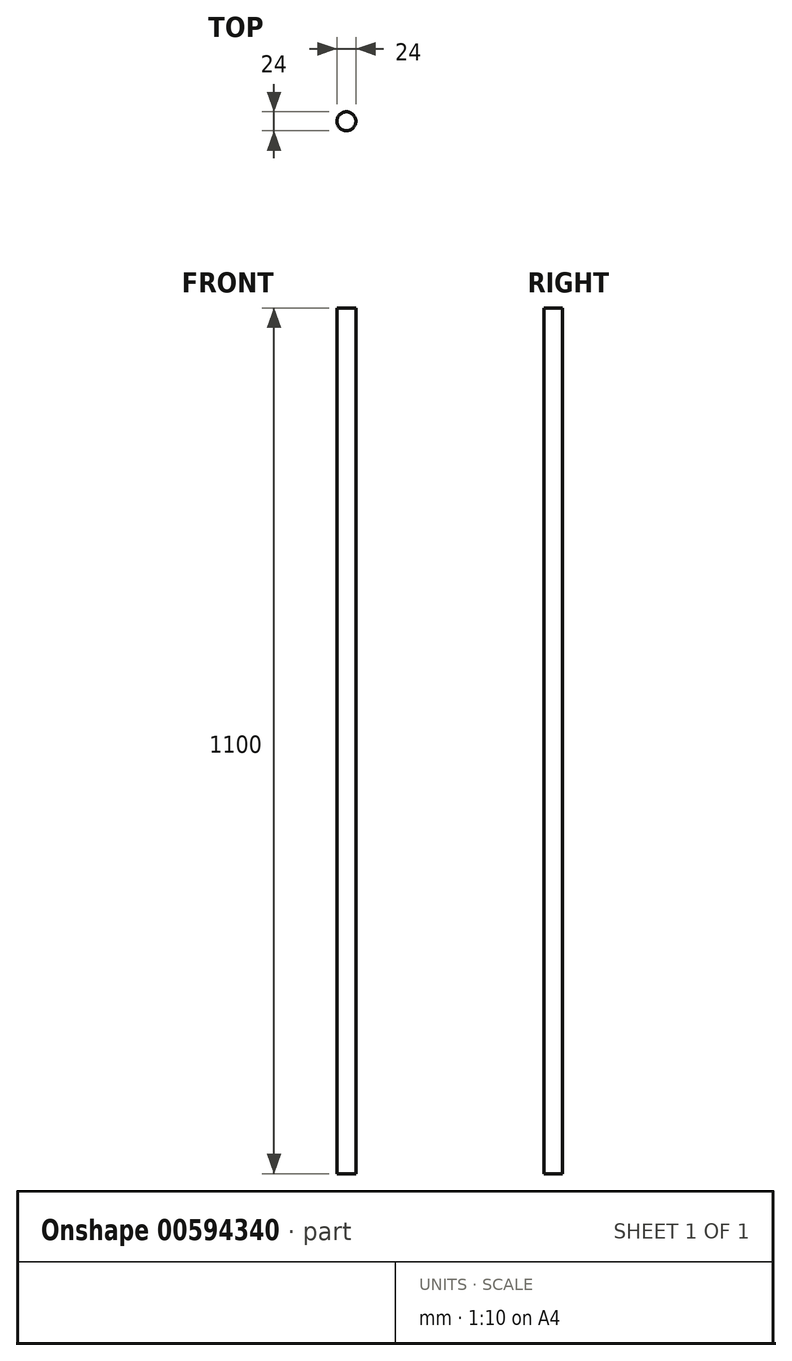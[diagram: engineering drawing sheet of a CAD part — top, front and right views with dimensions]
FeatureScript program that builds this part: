
annotation { "Feature Type Name" : "Feature", "Feature Type Description" : "" }
export const myFeature = defineFeature(function(context is Context, id is Id, definition is map)
    precondition{}
    {
        {
            var Q0;
            Q0=qCreatedBy(makeId("Top.planeOp"),FACE);
            var sketch = newSketch(context, id + "F0", { "sketchPlane" : qUnion([Q0])});
            skCircle(sketch, "E0", {"center": v(0, 0) * mm, "radius": 12 * mm});
            skSolve(sketch);
        }
        {
            var Q0;
            Q0 = qSketchRegion(id + "F0", true);
            extrude(context, id + "F1", {"entities" : qUnion([Q0]), "depth" : 1100 * mm, "offsetDistance" : 25.4 * mm});
        }
    });
